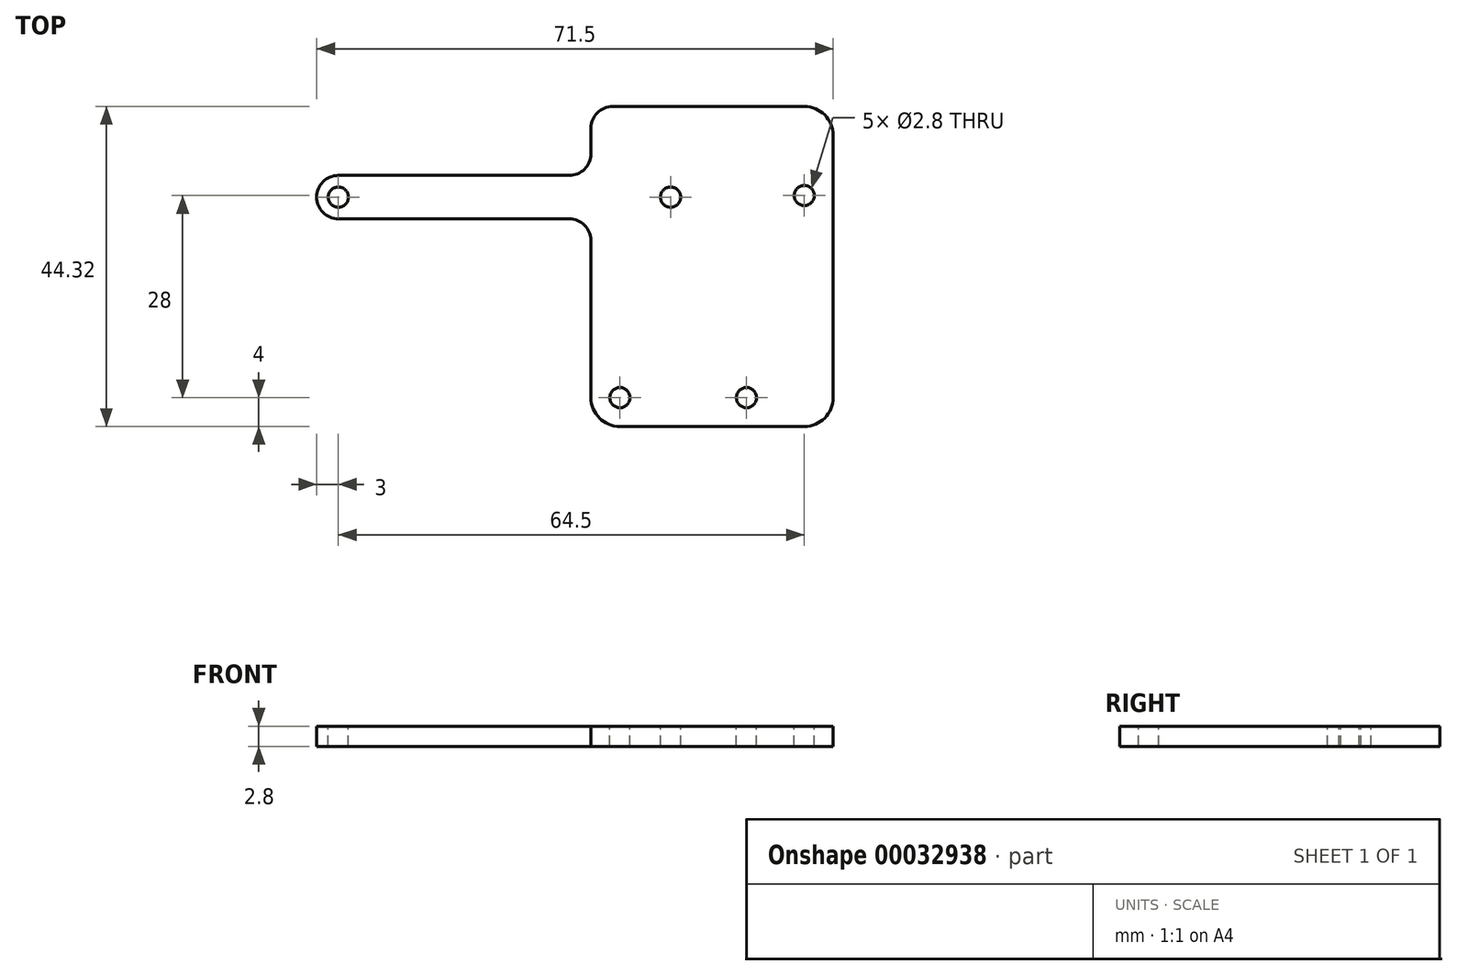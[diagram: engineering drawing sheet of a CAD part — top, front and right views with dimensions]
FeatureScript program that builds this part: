
annotation { "Feature Type Name" : "Feature", "Feature Type Description" : "" }
export const myFeature = defineFeature(function(context is Context, id is Id, definition is map)
    precondition{}
    {
        {
            var Q0;
            Q0=qCreatedBy(makeId("Top.planeOp"),FACE);
            var sketch = newSketch(context, id + "F0", { "sketchPlane" : qUnion([Q0])});
            skLineSegment(sketch, "E0.rect.bottom", {"start": v(5.82, -11.88) * mm, "end": v(-5.83, -11.88) * mm});
            skLineSegment(sketch, "E0.rect.top", {"start": v(5.83, 11.88) * mm, "end": v(-5.82, 11.88) * mm});
            skLineSegment(sketch, "E0.rect.left", {"start": v(5.82, -11.88) * mm, "end": v(5.83, 11.88) * mm});
            skLineSegment(sketch, "E0.rect.right", {"start": v(-5.83, -11.88) * mm, "end": v(-5.82, 11.87) * mm});
            skPoint(sketch, "E0.rect.middle", {"position": v(0, 0) * mm});
            skSolve(sketch);
        }
        {
            var Q0;
            Q0=qSketchRegion(id+"F0",true);
            extrude(context, id + "F1", {"entities" : qUnion([Q0]), "depth" : 20.4 * mm});
        }
        {
            var Q0;
            Q0=makeQuery(id+"F1.opExtrude","CAP_FACE",FACE,{"disambiguationData":[OSD([sQuery(id+"F0.wireOp",EDGE,"E0.rect.bottom"),sQuery(id+"F0.wireOp",EDGE,"E0.rect.top"),sQuery(id+"F0.wireOp",EDGE,"E0.rect.left"),sQuery(id+"F0.wireOp",EDGE,"E0.rect.right")])],"isStart":false});
            var sketch = newSketch(context, id + "F2", { "sketchPlane" : qUnion([Q0])});
            skArc(sketch, "E1", {"start": v(5.83, 7.59) * mm, "mid": v(0, 11.88) * mm, "end": v(-5.83, 7.59) * mm});
            skLineSegment(sketch, "E2", {"start": v(5.83, 7.59) * mm, "end": v(5.83, 3.96) * mm});
            skLineSegment(sketch, "E3.MirrorCS", {"start": v(-5.83, 7.59) * mm, "end": v(-5.83, 3.96) * mm});
            skArc(sketch, "E4.trimOffspring", {"start": v(-5.83, 3.96) * mm, "mid": v(-4.78, 1.98) * mm, "end": v(-3.09, 0.51) * mm});
            skArc(sketch, "E5", {"start": v(-3.09, 0.51) * mm, "mid": v(0, -3.1) * mm, "end": v(3.09, 0.51) * mm});
            skArc(sketch, "E6.trimOffspring", {"start": v(3.09, 0.51) * mm, "mid": v(4.78, 1.98) * mm, "end": v(5.83, 3.96) * mm});
            skSolve(sketch);
        }
        {
            var Q0;
            Q0=qSketchRegion(id+"F2",true);
            extrude(context, id + "F3", {"entities" : qUnion([Q0]), "operationType" : NewBodyOperationType.ADD, "depth" : 6 * mm});
        }
        {
            var Q0;
            {var subQ0=sQuery(id+"F0.wireOp",EDGE,"E0.rect.bottom");var subQ1=sQuery(id+"F0.wireOp",EDGE,"E0.rect.left");var subQ2=sQuery(id+"F0.wireOp",EDGE,"E0.rect.right");Q0=makeQuery(id+"F3.boolean.opBoolean","SPLIT",FACE,{"disambiguationData":[TD([makeQuery(id+"F1.opExtrude","SWEPT_FACE",FACE,{"disambiguationData":[OSD([subQ0])]}),makeQuery(id+"F1.opExtrude","SWEPT_FACE",FACE,{"disambiguationData":[OSD([subQ1])]}),makeQuery(id+"F1.opExtrude","SWEPT_FACE",FACE,{"disambiguationData":[OSD([subQ2])]}),makeQuery(id+"F3.opExtrude","SWEPT_FACE",FACE,{"disambiguationData":[OSD([sQuery(id+"F2.wireOp",EDGE,"E2")])]}),makeQuery(id+"F3.opExtrude","SWEPT_FACE",FACE,{"disambiguationData":[OSD([sQuery(id+"F2.wireOp",EDGE,"E3.MirrorCS")])]}),makeQuery(id+"F3.opExtrude","SWEPT_FACE",FACE,{"disambiguationData":[OSD([sQuery(id+"F2.wireOp",EDGE,"E4.trimOffspring")])]}),makeQuery(id+"F3.opExtrude","SWEPT_FACE",FACE,{"disambiguationData":[OSD([sQuery(id+"F2.wireOp",EDGE,"E5")])]}),makeQuery(id+"F3.opExtrude","SWEPT_FACE",FACE,{"disambiguationData":[OSD([sQuery(id+"F2.wireOp",EDGE,"E6.trimOffspring")])]})])],"derivedFrom":makeQuery(id+"F1.opExtrude","CAP_FACE",FACE,{"disambiguationData":[OSD([subQ0,sQuery(id+"F0.wireOp",EDGE,"E0.rect.top"),subQ1,subQ2])],"isStart":false})});}
            var sketch = newSketch(context, id + "F4", { "sketchPlane" : qUnion([Q0])});
            skLineSegment(sketch, "E7.bottom", {"start": v(-5.83, -11.88) * mm, "end": v(5.82, -11.88) * mm});
            skLineSegment(sketch, "E7.top", {"start": v(-5.83, -16.08) * mm, "end": v(5.82, -16.08) * mm});
            skLineSegment(sketch, "E7.left", {"start": v(-5.83, -11.88) * mm, "end": v(-5.83, -16.08) * mm});
            skLineSegment(sketch, "E7.right", {"start": v(5.82, -11.88) * mm, "end": v(5.82, -16.08) * mm});
            skLineSegment(sketch, "E8.MirrorCS", {"start": v(-5.83, 11.88) * mm, "end": v(-5.83, 16.08) * mm});
            skLineSegment(sketch, "E9.MirrorCS", {"start": v(-5.83, 16.08) * mm, "end": v(5.82, 16.08) * mm});
            skLineSegment(sketch, "E10.MirrorCS", {"start": v(5.82, 11.88) * mm, "end": v(5.82, 16.08) * mm});
            skLineSegment(sketch, "E11.MirrorCS", {"start": v(-5.83, 11.88) * mm, "end": v(5.82, 11.88) * mm});
            skSolve(sketch);
        }
        {
            var Q0;
            Q0=makeQuery(id+"F4.imprint","IMPRINT",FACE,{"disambiguationData":[TD([[makeQuery(id+"F4.imprint","IMPRINT",EDGE,{"derivedFrom":sQuery(id+"F4.wireOp",EDGE,"E7.bottom")}),1.0]])]});
            var Q1;
            Q1=makeQuery(id+"F4.imprint","IMPRINT",FACE,{"disambiguationData":[TD([[makeQuery(id+"F4.imprint","IMPRINT",EDGE,{"derivedFrom":sQuery(id+"F4.wireOp",EDGE,"E8.MirrorCS")}),-1.0]])]});
            extrude(context, id + "F5", {"entities" : qUnion([Q0, Q1]), "operationType" : NewBodyOperationType.ADD, "oppositeDirection" : true, "depth" : 2.8 * mm, "hasSecondDirection" : true, "secondDirectionOppositeDirection" : true, "secondDirectionDepth" : .8 * mm});
        }
        {
            var Q0;
            {var subQ0=sQuery(id+"F0.wireOp",EDGE,"E0.rect.top");var subQ1=sQuery(id+"F0.wireOp",EDGE,"E0.rect.left");Q0=makeQuery(id+"F5.boolean.opBoolean","SPLIT",EDGE,{"disambiguationData":[TD([makeQuery(id+"F1.opExtrude","CAP_FACE",FACE,{"disambiguationData":[OSD([sQuery(id+"F0.wireOp",EDGE,"E0.rect.bottom"),subQ0,subQ1,sQuery(id+"F0.wireOp",EDGE,"E0.rect.right")])],"isStart":true})])],"derivedFrom":makeQuery(id+"F1.opExtrude","SWEPT_EDGE",EDGE,{"disambiguationData":[OSD([subQ0,subQ1])]})});}
            var Q1;
            {var subQ0=sQuery(id+"F0.wireOp",EDGE,"E0.rect.bottom");var subQ1=sQuery(id+"F0.wireOp",EDGE,"E0.rect.left");Q1=makeQuery(id+"F5.boolean.opBoolean","SPLIT",EDGE,{"disambiguationData":[TD([makeQuery(id+"F1.opExtrude","CAP_FACE",FACE,{"disambiguationData":[OSD([subQ0,sQuery(id+"F0.wireOp",EDGE,"E0.rect.top"),subQ1,sQuery(id+"F0.wireOp",EDGE,"E0.rect.right")])],"isStart":true})])],"derivedFrom":makeQuery(id+"F1.opExtrude","SWEPT_EDGE",EDGE,{"disambiguationData":[OSD([subQ0,subQ1])]})});}
            var Q2;
            {var subQ0=sQuery(id+"F0.wireOp",EDGE,"E0.rect.bottom");var subQ1=sQuery(id+"F0.wireOp",EDGE,"E0.rect.right");Q2=makeQuery(id+"F5.boolean.opBoolean","SPLIT",EDGE,{"disambiguationData":[TD([makeQuery(id+"F1.opExtrude","CAP_FACE",FACE,{"disambiguationData":[OSD([subQ0,sQuery(id+"F0.wireOp",EDGE,"E0.rect.top"),sQuery(id+"F0.wireOp",EDGE,"E0.rect.left"),subQ1])],"isStart":true})])],"derivedFrom":makeQuery(id+"F1.opExtrude","SWEPT_EDGE",EDGE,{"disambiguationData":[OSD([subQ0,subQ1])]})});}
            var Q3;
            {var subQ0=sQuery(id+"F0.wireOp",EDGE,"E0.rect.top");var subQ1=sQuery(id+"F0.wireOp",EDGE,"E0.rect.right");Q3=makeQuery(id+"F5.boolean.opBoolean","SPLIT",EDGE,{"disambiguationData":[TD([makeQuery(id+"F1.opExtrude","CAP_FACE",FACE,{"disambiguationData":[OSD([sQuery(id+"F0.wireOp",EDGE,"E0.rect.bottom"),subQ0,sQuery(id+"F0.wireOp",EDGE,"E0.rect.left"),subQ1])],"isStart":true})])],"derivedFrom":makeQuery(id+"F1.opExtrude","SWEPT_EDGE",EDGE,{"disambiguationData":[OSD([subQ0,subQ1])]})});}
            fillet(context, id + "F6", {"entities" : qUnion([Q0, Q1, Q2, Q3]), "radius" : .5 * mm, "tangentPropagation" : true, "allowEdgeOverflow" : false});
        }
        {
            var Q0;
            Q0=makeQuery(id+"F5.opExtrude","SWEPT_EDGE",EDGE,{"disambiguationData":[OSD([sQuery(id+"F4.wireOp",EDGE,"E8.MirrorCS"),sQuery(id+"F4.wireOp",EDGE,"E9.MirrorCS")])]});
            var Q1;
            Q1=makeQuery(id+"F5.opExtrude","SWEPT_EDGE",EDGE,{"disambiguationData":[OSD([sQuery(id+"F4.wireOp",EDGE,"E9.MirrorCS"),sQuery(id+"F4.wireOp",EDGE,"E10.MirrorCS")])]});
            var Q2;
            Q2=makeQuery(id+"F5.opExtrude","SWEPT_EDGE",EDGE,{"disambiguationData":[OSD([sQuery(id+"F4.wireOp",EDGE,"E7.top"),sQuery(id+"F4.wireOp",EDGE,"E7.right")])]});
            var Q3;
            Q3=makeQuery(id+"F5.opExtrude","SWEPT_EDGE",EDGE,{"disambiguationData":[OSD([sQuery(id+"F4.wireOp",EDGE,"E7.top"),sQuery(id+"F4.wireOp",EDGE,"E7.left")])]});
            fillet(context, id + "F7", {"entities" : qUnion([Q0, Q1, Q2, Q3]), "radius" : 1 * mm, "tangentPropagation" : true, "allowEdgeOverflow" : false});
        }
        {
            var Q0;
            Q0=makeQuery(id+"F3.opExtrude","CAP_FACE",FACE,{"disambiguationData":[OSD([sQuery(id+"F2.wireOp",EDGE,"E1"),sQuery(id+"F2.wireOp",EDGE,"E2"),sQuery(id+"F2.wireOp",EDGE,"E3.MirrorCS"),sQuery(id+"F2.wireOp",EDGE,"E4.trimOffspring"),sQuery(id+"F2.wireOp",EDGE,"E5"),sQuery(id+"F2.wireOp",EDGE,"E6.trimOffspring")])],"isStart":false});
            var sketch = newSketch(context, id + "F8", { "sketchPlane" : qUnion([Q0])});
            skLineSegment(sketch, "E12", {"start": v(-5.83, 3.96) * mm, "end": v(-5.83, 5.78) * mm});
            skLineSegment(sketch, "E13.rect.left", {"start": v(22.5, 18.32) * mm, "end": v(22.5, -26) * mm});
            skPoint(sketch, "E13.rect.middle", {"position": v(0, 0) * mm});
            skLineSegment(sketch, "E14", {"start": v(1.61, 18.32) * mm, "end": v(-8.03, 18.32) * mm});
            skLineSegment(sketch, "E15", {"start": v(-11.03, 15.32) * mm, "end": v(-11.03, 11.78) * mm});
            skPoint(sketch, "E16.orphan", {"position": v(-22.5, 30) * mm});
            skPoint(sketch, "E17.visualSharp", {"position": v(-11.03, -26) * mm});
            skPoint(sketch, "E18.visualSharp", {"position": v(4.61, 18.32) * mm});
            skPoint(sketch, "E19.visualSharp", {"position": v(-11.03, 18.32) * mm});
            skArc(sketch, "E19.filletArc", {"start": v(-8.03, 18.32) * mm, "mid": v(-10.15, 17.44) * mm, "end": v(-11.03, 15.32) * mm});
            skLineSegment(sketch, "E20", {"start": v(0, 5.78) * mm, "end": v(-46, 5.78) * mm, "construction": true});
            skCircle(sketch, "E21", {"center": v(-46, 5.78) * mm, "radius": 1.4 * mm});
            skArc(sketch, "E22", {"start": v(-46, 8.78) * mm, "mid": v(-49, 5.78) * mm, "end": v(-46, 2.78) * mm});
            skLineSegment(sketch, "E23", {"start": v(-46, 2.78) * mm, "end": v(-14.03, 2.78) * mm});
            skLineSegment(sketch, "E24.MirrorCS", {"start": v(-46, 8.78) * mm, "end": v(-14.03, 8.78) * mm});
            skLineSegment(sketch, "E25.trimOffspring", {"start": v(-11.03, -0.22) * mm, "end": v(-11.03, -15.07) * mm});
            skPoint(sketch, "E26.visualSharp", {"position": v(-11.03, 8.78) * mm});
            skArc(sketch, "E26.filletArc", {"start": v(-14.03, 8.78) * mm, "mid": v(-11.9, 9.65) * mm, "end": v(-11.03, 11.78) * mm});
            skPoint(sketch, "E27.visualSharp", {"position": v(-11.03, 2.78) * mm});
            skArc(sketch, "E27.filletArc", {"start": v(-11.03, -0.22) * mm, "mid": v(-11.9, 1.9) * mm, "end": v(-14.03, 2.77) * mm});
            skLineSegment(sketch, "E28", {"start": v(-11.03, -15.07) * mm, "end": v(-11.03, -26) * mm});
            skLineSegment(sketch, "E29", {"start": v(-11.03, -26) * mm, "end": v(22.5, -26) * mm});
            skLineSegment(sketch, "E30.bottom", {"start": v(-11.03, -26) * mm, "end": v(-7.03, -26) * mm, "construction": true});
            skLineSegment(sketch, "E30.top", {"start": v(-11.03, -22) * mm, "end": v(-7.03, -22) * mm, "construction": true});
            skLineSegment(sketch, "E30.left", {"start": v(-11.03, -26) * mm, "end": v(-11.03, -22) * mm, "construction": true});
            skLineSegment(sketch, "E30.right", {"start": v(-7.03, -26) * mm, "end": v(-7.03, -22) * mm, "construction": true});
            skCircle(sketch, "E31", {"center": v(-7.03, -22) * mm, "radius": 1.4 * mm});
            skLineSegment(sketch, "E32.bottom", {"start": v(22.5, -26) * mm, "end": v(18.5, -26) * mm, "construction": true});
            skLineSegment(sketch, "E32.top", {"start": v(22.5, -22) * mm, "end": v(18.5, -22) * mm, "construction": true});
            skLineSegment(sketch, "E32.left", {"start": v(22.5, -26) * mm, "end": v(22.5, -22) * mm, "construction": true});
            skLineSegment(sketch, "E32.right", {"start": v(18.5, -26) * mm, "end": v(18.5, -22) * mm, "construction": true});
            skCircle(sketch, "E33", {"center": v(18.5, -22) * mm, "radius": 1.4 * mm, "construction": true});
            skCircle(sketch, "E34", {"center": v(0, 5.78) * mm, "radius": 1.4 * mm});
            skPoint(sketch, "E35.orphan", {"position": v(-5.83, 7.59) * mm});
            skPoint(sketch, "E36.MirrorCS.end.orphan", {"position": v(5.83, 7.59) * mm});
            skPoint(sketch, "E37.end.orphan", {"position": v(5.83, 3.96) * mm});
            skLineSegment(sketch, "E38", {"start": v(1.61, 18.32) * mm, "end": v(22.5, 18.32) * mm});
            skCircle(sketch, "E39", {"center": v(10.5, -22) * mm, "radius": 1.4 * mm});
            skCircle(sketch, "E40", {"center": v(18.5, 6) * mm, "radius": 1.4 * mm});
            skSolve(sketch);
        }
        {
            var Q0;
            Q0=qSketchRegion(id+"F8",true);
            extrude(context, id + "F9", {"entities" : qUnion([Q0]), "oppositeDirection" : true, "depth" : 2.8 * mm});
        }
        {
            var Q0;
            Q0=makeQuery(id+"F9.opExtrude","SWEPT_EDGE",EDGE,{"disambiguationData":[OSD([sQuery(id+"F8.wireOp",EDGE,"E13.rect.top"),sQuery(id+"F8.wireOp",EDGE,"E13.rect.right")])]});
            var Q1;
            Q1=makeQuery(id+"F9.opExtrude","SWEPT_EDGE",EDGE,{"disambiguationData":[OSD([sQuery(id+"F8.wireOp",EDGE,"E13.rect.bottom"),sQuery(id+"F8.wireOp",EDGE,"E13.rect.right")])]});
            var Q2;
            Q2=makeQuery(id+"F9.opExtrude","SWEPT_EDGE",EDGE,{"disambiguationData":[OSD([sQuery(id+"F8.wireOp",EDGE,"E13.rect.bottom"),sQuery(id+"F8.wireOp",EDGE,"E13.rect.left")])]});
            var Q3;
            Q3=makeQuery(id+"F9.opExtrude","SWEPT_EDGE",EDGE,{"disambiguationData":[OSD([sQuery(id+"F8.wireOp",EDGE,"E13.rect.top"),sQuery(id+"F8.wireOp",EDGE,"E13.rect.left")])]});
            var Q4;
            Q4=makeQuery(id+"F9.opExtrude","SWEPT_EDGE",EDGE,{"disambiguationData":[OSD([sQuery(id+"F8.wireOp",EDGE,"E28"),sQuery(id+"F8.wireOp",EDGE,"E29")])]});
            fillet(context, id + "F10", {"entities" : qUnion([Q0, Q1, Q2, Q3, Q4]), "radius" : 4 * mm, "tangentPropagation" : true, "allowEdgeOverflow" : false});
        }
        {
            var Q0;
            Q0=makeQuery(id+"F9.opExtrude","SWEPT_BODY",BODY,{"disambiguationData":[OSD([sQuery(id+"F8.wireOp",EDGE,"E37"),sQuery(id+"F8.wireOp",EDGE,"a7b3f6ed-c376-49eb-9cb2-135e59594782"),sQuery(id+"F8.wireOp",EDGE,"E12"),sQuery(id+"F8.wireOp",EDGE,"E36.MirrorCS"),sQuery(id+"F8.wireOp",EDGE,"d2d63f77-5541-4a7f-8d51-7ca97668e1f1.trimOffspring"),sQuery(id+"F8.wireOp",EDGE,"b199d975-cfa0-4d79-aa76-c9a82bb31a59.trimOffspring"),sQuery(id+"F8.wireOp",EDGE,"E13.rect.bottom"),sQuery(id+"F8.wireOp",EDGE,"E13.rect.top"),sQuery(id+"F8.wireOp",EDGE,"E13.rect.left"),sQuery(id+"F8.wireOp",EDGE,"E13.rect.right"),sQuery(id+"F8.wireOp",EDGE,"a12ce330-09d9-461c-8b2f-e163017ed208"),sQuery(id+"F8.wireOp",EDGE,"ce85554a-ae08-408d-bbdd-004999f886530.MirrorC"),sQuery(id+"F8.wireOp",EDGE,"74581e88-93ef-4e49-bf24-ccc966527bf30.MirrorC"),sQuery(id+"F8.wireOp",EDGE,"a9b9e684-8755-4f44-b45f-45d0958772250.MirrorC"),sQuery(id+"F8.wireOp",EDGE,"76930b9b-8da1-4d4d-b0e5-4a7641f42912"),sQuery(id+"F8.wireOp",EDGE,"f42893a9-d5a1-4c2e-96db-01520e8eb7290.MirrorC"),sQuery(id+"F8.wireOp",EDGE,"46118b25-6d7d-4224-8583-2d73bb83e9220.MirrorC"),sQuery(id+"F8.wireOp",EDGE,"b2e64fab-b84c-4731-9833-593c73ce0a330.MirrorC")])]});
            transform(context, id + "F11", {"entities" : qUnion([Q0]), "transformType" : TransformType.TRANSLATION_3D, "dx" : 0 * mm, "dy" : 0 * mm, "dz" : 0 * mm, "makeCopy" : true});
        }
        {
            var Q0;
            Q0=makeQuery(id+"F11.opPattern","COPY",BODY,{"derivedFrom":makeQuery(id+"F9.opExtrude","SWEPT_BODY",BODY,{"disambiguationData":[OSD([sQuery(id+"F8.wireOp",EDGE,"E37"),sQuery(id+"F8.wireOp",EDGE,"a7b3f6ed-c376-49eb-9cb2-135e59594782"),sQuery(id+"F8.wireOp",EDGE,"E12"),sQuery(id+"F8.wireOp",EDGE,"E36.MirrorCS"),sQuery(id+"F8.wireOp",EDGE,"d2d63f77-5541-4a7f-8d51-7ca97668e1f1.trimOffspring"),sQuery(id+"F8.wireOp",EDGE,"b199d975-cfa0-4d79-aa76-c9a82bb31a59.trimOffspring"),sQuery(id+"F8.wireOp",EDGE,"E13.rect.bottom"),sQuery(id+"F8.wireOp",EDGE,"E13.rect.top"),sQuery(id+"F8.wireOp",EDGE,"E13.rect.left"),sQuery(id+"F8.wireOp",EDGE,"E13.rect.right"),sQuery(id+"F8.wireOp",EDGE,"a12ce330-09d9-461c-8b2f-e163017ed208"),sQuery(id+"F8.wireOp",EDGE,"74581e88-93ef-4e49-bf24-ccc966527bf30.MirrorC"),sQuery(id+"F8.wireOp",EDGE,"a9b9e684-8755-4f44-b45f-45d0958772250.MirrorC"),sQuery(id+"F8.wireOp",EDGE,"76930b9b-8da1-4d4d-b0e5-4a7641f42912"),sQuery(id+"F8.wireOp",EDGE,"f42893a9-d5a1-4c2e-96db-01520e8eb7290.MirrorC"),sQuery(id+"F8.wireOp",EDGE,"b2e64fab-b84c-4731-9833-593c73ce0a330.MirrorC"),sQuery(id+"F8.wireOp",EDGE,"6dbd4985-7d77-4368-82c7-85e426a01a06"),sQuery(id+"F8.wireOp",EDGE,"E14"),sQuery(id+"F8.wireOp",EDGE,"E15"),sQuery(id+"F8.wireOp",EDGE,"8f80475a-625c-4095-acb9-1eab8cfb7864"),sQuery(id+"F8.wireOp",EDGE,"E17.filletArc"),sQuery(id+"F8.wireOp",EDGE,"E18.filletArc"),sQuery(id+"F8.wireOp",EDGE,"E19.filletArc")])]}),"instanceName":"1"});
            deleteBodies(context, id + "F12", {"entities" : qUnion([Q0])});
        }
        {
            var Q0;
            Q0=makeQuery(id+"F1.opExtrude","SWEPT_BODY",BODY,{"disambiguationData":[OSD([sQuery(id+"F0.wireOp",EDGE,"E0.rect.bottom"),sQuery(id+"F0.wireOp",EDGE,"E0.rect.top"),sQuery(id+"F0.wireOp",EDGE,"E0.rect.left"),sQuery(id+"F0.wireOp",EDGE,"E0.rect.right")])]});
            deleteBodies(context, id + "F13", {"entities" : qUnion([Q0])});
        }
    });
